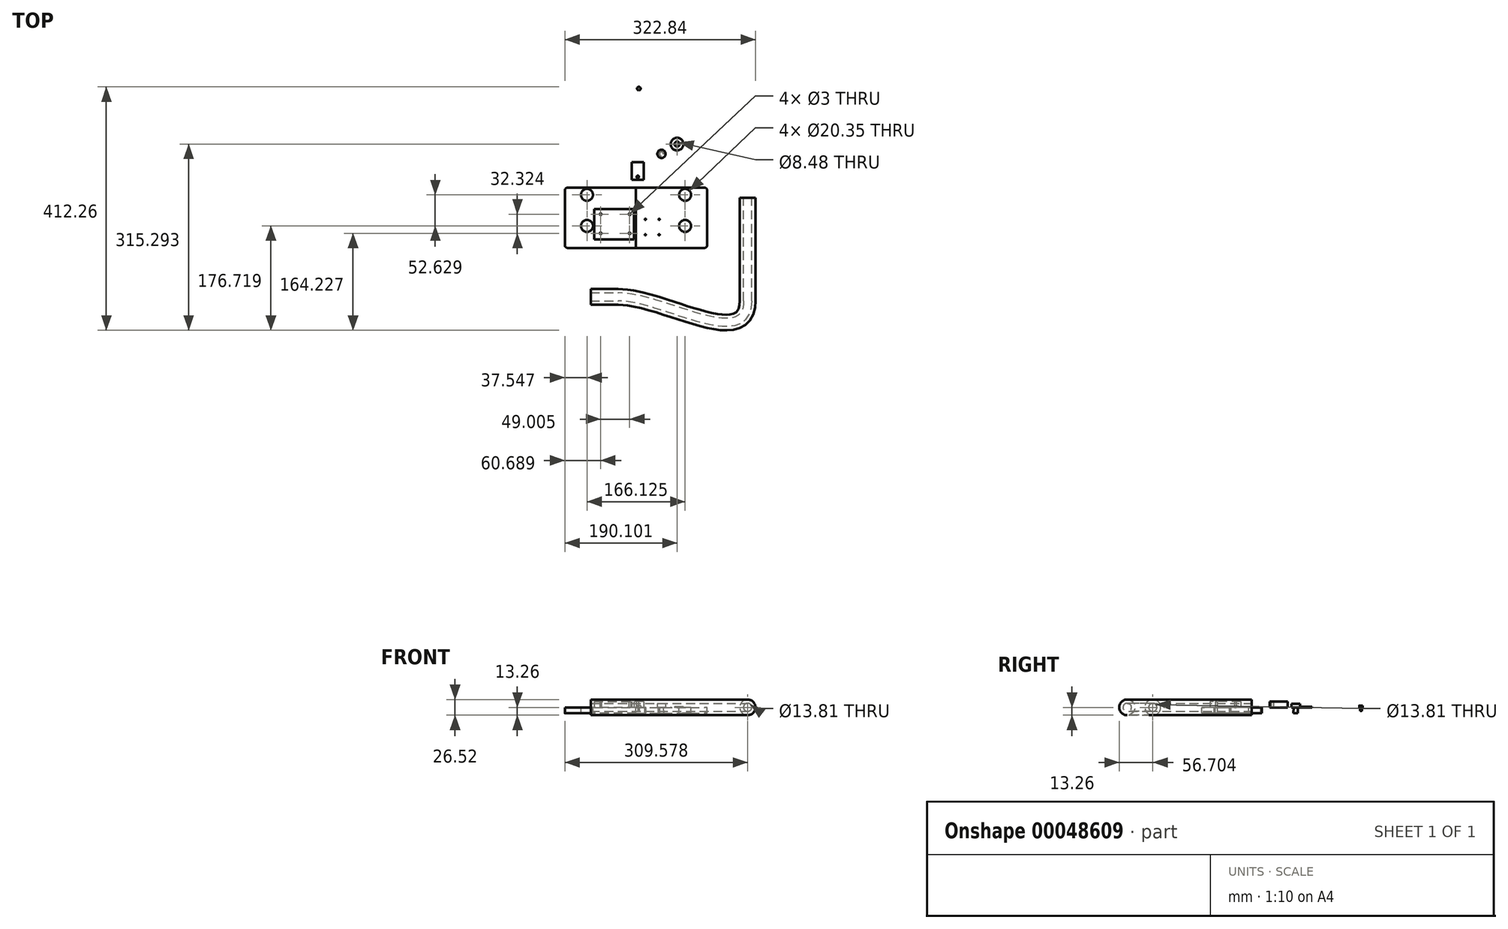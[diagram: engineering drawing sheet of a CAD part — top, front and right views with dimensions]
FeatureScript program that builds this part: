
annotation { "Feature Type Name" : "Feature", "Feature Type Description" : "" }
export const myFeature = defineFeature(function(context is Context, id is Id, definition is map)
    precondition{}
    {
        {
            var Q0;
            Q0=qCreatedBy(makeId("Top.planeOp"),FACE);
            var sketch = newSketch(context, id + "F17", { "sketchPlane" : qUnion([Q0])});
            skLineSegment(sketch, "E0.bottom", {"start": v(10, -15) * mm, "end": v(-10, -15) * mm});
            skLineSegment(sketch, "E0.top", {"start": v(10, 15) * mm, "end": v(-10, 15) * mm});
            skLineSegment(sketch, "E0.left", {"start": v(10, -15) * mm, "end": v(10, 15) * mm});
            skLineSegment(sketch, "E0.right", {"start": v(-10, -15) * mm, "end": v(-10, 15) * mm});
            skLineSegment(sketch, "E1", {"start": v(-10, 15) * mm, "end": v(10, -15) * mm, "construction": true});
            skSolve(sketch);
        }
        {
            var Q0;
            Q0 = qSketchRegion(id + "F17", true);
            extrude(context, id + "F18", {"entities" : qUnion([Q0]), "depth" : 10 * mm});
        }
        {
            var Q0;
            Q0=qCreatedBy(makeId("Top.planeOp"),FACE);
            var sketch = newSketch(context, id + "F19", { "sketchPlane" : qUnion([Q0])});
            skCircle(sketch, "E2", {"center": v(40.06, 28.89) * mm, "radius": 7.04 * mm});
            skSolve(sketch);
        }
        {
            var Q0;
            Q0=makeQuery(id+"F19.imprint","IMPRINT",FACE,{"disambiguationData":[TD([[makeQuery(id+"F19.imprint","IMPRINT",EDGE,{"derivedFrom":sQuery(id+"F19.wireOp",EDGE,"E2")}),1.0]])]});
            extrude(context, id + "F20", {"entities" : qUnion([Q0]), "depth" : 6 * mm});
        }
        {
            var Q0;
            Q0=makeQuery(id+"F20.opExtrude","CAP_FACE",FACE,{"disambiguationData":[OSD([sQuery(id+"F19.wireOp",EDGE,"E2")])],"isStart":true});
            var sketch = newSketch(context, id + "F0", { "sketchPlane" : qUnion([Q0])});
            skCircle(sketch, "E3", {"center": v(40.06, -28.89) * mm, "radius": 3.3 * mm});
            skSolve(sketch);
        }
        {
            var Q0;
            Q0 = qSketchRegion(id + "F0", true);
            extrude(context, id + "F21", {"entities" : qUnion([Q0]), "operationType" : NewBodyOperationType.ADD, "depth" : 10 * mm, "hasDraft" : true, "draftAngle" : 3 * degree});
        }
        {
            var Q0;
            Q0=makeQuery(id+"F18.opExtrude","CAP_FACE",FACE,{"disambiguationData":[OSD([sQuery(id+"F17.wireOp",EDGE,"E0.bottom"),sQuery(id+"F17.wireOp",EDGE,"E0.top"),sQuery(id+"F17.wireOp",EDGE,"E0.left"),sQuery(id+"F17.wireOp",EDGE,"E0.right")])],"isStart":false});
            var sketch = newSketch(context, id + "F1", { "sketchPlane" : qUnion([Q0])});
            skCircle(sketch, "E4", {"center": v(0, -10) * mm, "radius": 2 * mm});
            skSolve(sketch);
        }
        {
            var Q0;
            Q0 = qSketchRegion(id + "F1", true);
            extrude(context, id + "F22", {"entities" : qUnion([Q0]), "operationType" : NewBodyOperationType.REMOVE, "endBound" : BoundingType.THROUGH_ALL, "oppositeDirection" : true, "depth" : 25 * mm});
        }
        {
            var Q0;
            Q0=qCreatedBy(makeId("Top.planeOp"),FACE);
            var sketch = newSketch(context, id + "F2", { "sketchPlane" : qUnion([Q0])});
            skCircle(sketch, "E5", {"center": v(66.46, 45.41) * mm, "radius": 10.8 * mm});
            skCircle(sketch, "E6", {"center": v(66.46, 45.41) * mm, "radius": 4.24 * mm});
            skSolve(sketch);
        }
        {
            var Q0;
            Q0=makeQuery(id+"F2.imprint","IMPRINT",FACE,{"disambiguationData":[TD([[makeQuery(id+"F2.imprint","IMPRINT",EDGE,{"derivedFrom":sQuery(id+"F2.wireOp",EDGE,"E5")}),1.0]])]});
            var Q1;
            Q1=sQuery(id+"F2.wireOp",EDGE,"E6");
            extrude(context, id + "F23", {"entities" : qUnion([Q0]), "surfaceEntities" : qUnion([Q1]), "depth" : 1 * mm});
        }
        {
            var Q0;
            Q0=qCreatedBy(makeId("Top.planeOp"),FACE);
            var sketch = newSketch(context, id + "F24", { "sketchPlane" : qUnion([Q0])});
            skLineSegment(sketch, "E7", {"start": v(15.09, -40.53) * mm, "end": v(80.03, -40.53) * mm, "construction": true});
            skLineSegment(sketch, "E8", {"start": v(80.03, -40.53) * mm, "end": v(80.03, -93.16) * mm, "construction": true});
            skLineSegment(sketch, "E9", {"start": v(80.03, -93.16) * mm, "end": v(55.86, -93.16) * mm, "construction": true});
            skLineSegment(sketch, "E10", {"start": v(55.86, -93.16) * mm, "end": v(55.86, -62.33) * mm, "construction": true});
            skLineSegment(sketch, "E11", {"start": v(55.86, -62.33) * mm, "end": v(15.09, -62.33) * mm, "construction": true});
            skLineSegment(sketch, "E12", {"start": v(15.09, -62.33) * mm, "end": v(15.09, -40.53) * mm, "construction": true});
            skLineSegment(sketch, "E13.bottom", {"start": v(-3.03, -28.4) * mm, "end": v(117.58, -28.4) * mm});
            skLineSegment(sketch, "E13.top", {"start": v(-3.03, -130.43) * mm, "end": v(117.58, -130.43) * mm});
            skLineSegment(sketch, "E13.left", {"start": v(-3.03, -28.4) * mm, "end": v(-3.03, -130.43) * mm});
            skLineSegment(sketch, "E13.right", {"start": v(117.58, -28.4) * mm, "end": v(117.58, -130.43) * mm});
            skSolve(sketch);
        }
        {
            var Q0;
            Q0=qCreatedBy(makeId("Top.planeOp"),FACE);
            var sketch = newSketch(context, id + "F25", { "sketchPlane" : qUnion([Q0])});
            skCircle(sketch, "E14", {"center": v(80.03, -93.16) * mm, "radius": 10.18 * mm});
            skCircle(sketch, "E15", {"center": v(80.03, -40.53) * mm, "radius": 10.18 * mm});
            skSolve(sketch);
        }
        {
            var Q0;
            Q0=makeQuery(id+"F24.imprint","IMPRINT",FACE,{"disambiguationData":[TD([[makeQuery(id+"F24.imprint","IMPRINT",EDGE,{"derivedFrom":sQuery(id+"F24.wireOp",EDGE,"E13.bottom")}),-1.0]])]});
            extrude(context, id + "F3", {"entities" : qUnion([Q0]), "oppositeDirection" : true, "depth" : 10 * mm});
        }
        {
            var Q0;
            Q0 = qSketchRegion(id + "F25", true);
            extrude(context, id + "F26", {"entities" : qUnion([Q0]), "operationType" : NewBodyOperationType.REMOVE, "oppositeDirection" : true, "depth" : 25 * mm});
        }
        {
            var Q0;
            Q0=makeQuery(id+"F3.opExtrude","SWEPT_EDGE",EDGE,{"disambiguationData":[OSD([sQuery(id+"F24.wireOp",EDGE,"E13.top"),sQuery(id+"F24.wireOp",EDGE,"E13.right")])]});
            var Q1;
            Q1=makeQuery(id+"F3.opExtrude","SWEPT_EDGE",EDGE,{"disambiguationData":[OSD([sQuery(id+"F24.wireOp",EDGE,"E13.bottom"),sQuery(id+"F24.wireOp",EDGE,"E13.right")])]});
            fillet(context, id + "F4", {"entities" : qUnion([Q0, Q1]), "radius" : 5 * mm, "tangentPropagation" : true, "allowEdgeOverflow" : false});
        }
        {
            var Q0;
            Q0=makeQuery(id+"F3.opExtrude","SWEPT_BODY",BODY,{"disambiguationData":[OSD([sQuery(id+"F24.wireOp",EDGE,"E13.bottom"),sQuery(id+"F24.wireOp",EDGE,"E13.top"),sQuery(id+"F24.wireOp",EDGE,"E13.left"),sQuery(id+"F24.wireOp",EDGE,"E13.right")])]});
            var Q1;
            Q1=makeQuery(id+"F3.opExtrude","SWEPT_FACE",FACE,{"disambiguationData":[OSD([sQuery(id+"F24.wireOp",EDGE,"E13.left")])]});
            mirror(context, id + "F27", {"operationType" : NewBodyOperationType.ADD, "entities" : qUnion([Q0]), "mirrorPlane" : qUnion([Q1])});
        }
        {
            var Q0;
            Q0=qCreatedBy(makeId("Top.planeOp"),FACE);
            var sketch = newSketch(context, id + "F28", { "sketchPlane" : qUnion([Q0])});
            skLineSegment(sketch, "E16", {"start": v(-79.63, -213.18) * mm, "end": v(-33.15, -213.18) * mm});
            skLineSegment(sketch, "E17", {"start": v(185.94, -45.6) * mm, "end": v(185.94, -219.95) * mm});
            skFitSpline(sketch, "E18", {"points": [v(-33.15, -213.18) * mm, v(185.94, -219.95) * mm], "startDerivative": vector(229, 0) * mm, "endDerivative": vector(0, 258.85) * mm});
            skSolve(sketch);
        }
        {
            var Q0;
            Q0=sQuery(id+"F28.wireOp",VERTEX,"E16.start");
            var Q1;
            Q1=qCreatedBy(makeId("Right.planeOp"),FACE);
            cPlane(context, id + "F5", {"entities" : qUnion([Q0, Q1]), "cplaneType" : CPlaneType.PLANE_POINT, "offset" : 150 * mm, "width" : 150 * mm, "height" : 150 * mm});
        }
        {
            var Q0;
            Q0=qCreatedBy(id+"F5.planeOp",FACE);
            var sketch = newSketch(context, id + "F29", { "sketchPlane" : qUnion([Q0])});
            skCircle(sketch, "E19", {"center": v(-213.18, 0) * mm, "radius": 6.9 * mm});
            skCircle(sketch, "E20", {"center": v(-213.18, 0) * mm, "radius": 13.26 * mm});
            skSolve(sketch);
        }
        {
            var Q0;
            Q0 = qSketchRegion(id + "F29", true);
            var Q1;
            Q1=sQuery(id+"F28.wireOp",EDGE,"E16");
            var Q2;
            Q2=sQuery(id+"F28.wireOp",EDGE,"E18");
            var Q3;
            Q3=sQuery(id+"F28.wireOp",EDGE,"E17");
            sweep(context, id + "F30", {"profiles" : qUnion([Q0]), "path" : qUnion([Q1, Q2, Q3])});
        }
        {
            var Q0;
            {var subQ0=makeQuery(id+"F3.opExtrude","CAP_FACE",FACE,{"disambiguationData":[OSD([sQuery(id+"F24.wireOp",EDGE,"E13.bottom"),sQuery(id+"F24.wireOp",EDGE,"E13.top"),sQuery(id+"F24.wireOp",EDGE,"E13.left"),sQuery(id+"F24.wireOp",EDGE,"E13.right")])],"isStart":true});Q0=makeQuery(id+"F27.boolean.opBoolean","MERGE",FACE,{"derivedFrom":[subQ0,makeQuery(id+"F27.opPattern","COPY",FACE,{"derivedFrom":subQ0,"instanceName":"1"})]});}
            var sketch = newSketch(context, id + "F6", { "sketchPlane" : qUnion([Q0])});
            skLineSegment(sketch, "E21.bottom", {"start": v(-62.95, -73.33) * mm, "end": v(-13.95, -73.33) * mm});
            skLineSegment(sketch, "E21.top", {"start": v(-62.95, -105.65) * mm, "end": v(-13.95, -105.65) * mm});
            skLineSegment(sketch, "E21.left", {"start": v(-62.95, -73.33) * mm, "end": v(-62.95, -105.65) * mm});
            skLineSegment(sketch, "E21.right", {"start": v(-13.95, -73.33) * mm, "end": v(-13.95, -105.65) * mm});
            skSolve(sketch);
        }
        {
            var Q0;
            Q0=sQuery(id+"F6.wireOp",VERTEX,"E21.left.start");
            var Q1;
            Q1=sQuery(id+"F6.wireOp",VERTEX,"E21.right.start");
            var Q2;
            Q2=sQuery(id+"F6.wireOp",VERTEX,"E21.right.end");
            var Q3;
            Q3=sQuery(id+"F6.wireOp",VERTEX,"E21.top.start");
            var Q4;
            Q4=makeQuery(id+"F3.opExtrude","SWEPT_BODY",BODY,{"disambiguationData":[OSD([sQuery(id+"F24.wireOp",EDGE,"E13.bottom"),sQuery(id+"F24.wireOp",EDGE,"E13.top"),sQuery(id+"F24.wireOp",EDGE,"E13.left"),sQuery(id+"F24.wireOp",EDGE,"E13.right")])]});
            hole(context, id + "F7", {"style" : HoleStyle.C_BORE, "endStyle" : HoleEndStyle.THROUGH, "standardTappedOrClearance" : lookupTablePath({ "standard" : "ISO", "fit" : "Normal", "size" : "M3", "type" : "Clearance" }), "standardBlindInLast" : lookupTablePath({ "fit" : "Standard", "standard" : "ISO", "size" : "M3", "type" : "Clearance" }), "holeDiameter" : 3.3 * mm, "cBoreDiameter" : 6.5 * mm, "cBoreDepth" : 3 * mm, "isTappedThrough" : true, "tappedDepth" : 12 * mm, "tapClearance" : 3, "locations" : qUnion([Q0, Q1, Q2, Q3]), "scope" : qUnion([Q4])});
        }
        {
            var Q0;
            Q0=makeQuery(id+"F20.opExtrude","SWEPT_BODY",BODY,{"disambiguationData":[OSD([sQuery(id+"F19.wireOp",EDGE,"E2")])]});
            transform(context, id + "F8", {"entities" : qUnion([Q0]), "transformType" : TransformType.TRANSLATION_3D, "dx" : 0 * mm, "dy" : 0 * mm, "dz" : 0 * mm, "makeCopy" : true});
        }
        {
            var Q0;
            Q0=makeQuery(id+"F8.opPattern","COPY",BODY,{"derivedFrom":makeQuery(id+"F20.opExtrude","SWEPT_BODY",BODY,{"disambiguationData":[OSD([sQuery(id+"F19.wireOp",EDGE,"E2")])]}),"instanceName":"1"});
            deleteBodies(context, id + "F9", {"entities" : qUnion([Q0])});
        }
        {
            var Q0;
            Q0=qCreatedBy(makeId("Top.planeOp"),FACE);
            var sketch = newSketch(context, id + "F10", { "sketchPlane" : qUnion([Q0])});
            skCircle(sketch, "E22", {"center": v(1.78, 139.38) * mm, "radius": 3 * mm});
            skCircle(sketch, "E23", {"center": v(1.78, 139.38) * mm, "radius": 1.5 * mm});
            skSolve(sketch);
        }
        {
            var Q0;
            Q0=makeQuery(id+"F10.imprint","IMPRINT",FACE,{"disambiguationData":[TD([[makeQuery(id+"F10.imprint","IMPRINT",EDGE,{"derivedFrom":sQuery(id+"F10.wireOp",EDGE,"E23")}),1.0]])]});
            var Q1;
            Q1=makeQuery(id+"F10.imprint","IMPRINT",FACE,{"disambiguationData":[TD([[makeQuery(id+"F10.imprint","IMPRINT",EDGE,{"derivedFrom":sQuery(id+"F10.wireOp",EDGE,"E22")}),1.0]])]});
            extrude(context, id + "F11", {"entities" : qUnion([Q0, Q1]), "depth" : 3 * mm});
        }
        {
            var Q0;
            Q0=makeQuery(id+"F10.imprint","IMPRINT",FACE,{"disambiguationData":[TD([[makeQuery(id+"F10.imprint","IMPRINT",EDGE,{"derivedFrom":sQuery(id+"F10.wireOp",EDGE,"E23")}),1.0]])]});
            extrude(context, id + "F12", {"entities" : qUnion([Q0]), "operationType" : NewBodyOperationType.ADD, "oppositeDirection" : true, "depth" : 6 * mm});
        }
        {
            var Q0;
            {var subQ0=makeQuery(id+"F3.opExtrude","CAP_FACE",FACE,{"disambiguationData":[OSD([sQuery(id+"F24.wireOp",EDGE,"E13.bottom"),sQuery(id+"F24.wireOp",EDGE,"E13.top"),sQuery(id+"F24.wireOp",EDGE,"E13.left"),sQuery(id+"F24.wireOp",EDGE,"E13.right")])],"isStart":true});Q0=makeQuery(id+"F27.boolean.opBoolean","MERGE",FACE,{"derivedFrom":[subQ0,makeQuery(id+"F27.opPattern","COPY",FACE,{"derivedFrom":subQ0,"instanceName":"1"})]});}
            var sketch = newSketch(context, id + "F13", { "sketchPlane" : qUnion([Q0])});
            skLineSegment(sketch, "E24.bottom", {"start": v(-73.9, -64.37) * mm, "end": v(-6.2, -64.37) * mm});
            skLineSegment(sketch, "E24.top", {"start": v(-73.9, -116.08) * mm, "end": v(-6.2, -116.08) * mm});
            skLineSegment(sketch, "E24.left", {"start": v(-73.9, -64.37) * mm, "end": v(-73.9, -116.08) * mm});
            skLineSegment(sketch, "E24.right", {"start": v(-6.2, -64.37) * mm, "end": v(-6.2, -116.08) * mm});
            skCircle(sketch, "E25", {"center": v(-62.95, -73.33) * mm, "radius": 1.5 * mm});
            skCircle(sketch, "E26", {"center": v(-62.95, -105.65) * mm, "radius": 1.5 * mm});
            skCircle(sketch, "E27", {"center": v(-13.95, -73.33) * mm, "radius": 1.5 * mm});
            skCircle(sketch, "E28", {"center": v(-13.95, -105.65) * mm, "radius": 1.5 * mm});
            skSolve(sketch);
        }
        {
            var Q0;
            Q0=makeQuery(id+"F13.imprint","IMPRINT",FACE,{"disambiguationData":[TD([[makeQuery(id+"F13.imprint","IMPRINT",EDGE,{"derivedFrom":sQuery(id+"F13.wireOp",EDGE,"E24.bottom")}),-1.0]])]});
            var Q1;
            Q1=makeQuery(id+"F13.imprint","IMPRINT",FACE,{"disambiguationData":[TD([[makeQuery(id+"F13.imprint","IMPRINT",EDGE,{"derivedFrom":sQuery(id+"F13.wireOp",EDGE,"E26")}),-1.0]])]});
            var Q2;
            Q2=makeQuery(id+"F13.imprint","IMPRINT",FACE,{"disambiguationData":[TD([[makeQuery(id+"F13.imprint","IMPRINT",EDGE,{"derivedFrom":sQuery(id+"F13.wireOp",EDGE,"E27")}),-1.0]])]});
            var Q3;
            Q3=makeQuery(id+"F13.imprint","IMPRINT",FACE,{"disambiguationData":[TD([[makeQuery(id+"F13.imprint","IMPRINT",EDGE,{"derivedFrom":sQuery(id+"F13.wireOp",EDGE,"E28")}),-1.0]])]});
            var Q4;
            Q4=makeQuery(id+"F13.imprint","IMPRINT",FACE,{"disambiguationData":[TD([[makeQuery(id+"F13.imprint","IMPRINT",EDGE,{"derivedFrom":sQuery(id+"F13.wireOp",EDGE,"E25")}),-1.0]])]});
            extrude(context, id + "F14", {"entities" : qUnion([Q0, Q1, Q2, Q3, Q4]), "depth" : 10 * mm});
        }
        {
            var Q0;
            {var subQ0=makeQuery(id+"F3.opExtrude","CAP_FACE",FACE,{"disambiguationData":[OSD([sQuery(id+"F24.wireOp",EDGE,"E13.bottom"),sQuery(id+"F24.wireOp",EDGE,"E13.top"),sQuery(id+"F24.wireOp",EDGE,"E13.left"),sQuery(id+"F24.wireOp",EDGE,"E13.right")])],"isStart":true});Q0=makeQuery(id+"F27.boolean.opBoolean","MERGE",FACE,{"derivedFrom":[subQ0,makeQuery(id+"F27.opPattern","COPY",FACE,{"derivedFrom":subQ0,"instanceName":"1"})]});}
            var sketch = newSketch(context, id + "F15", { "sketchPlane" : qUnion([Q0])});
            skLineSegment(sketch, "E29.bottom", {"start": v(12.72, -81.79) * mm, "end": v(36.1, -81.79) * mm});
            skLineSegment(sketch, "E29.top", {"start": v(12.72, -108.12) * mm, "end": v(36.1, -108.12) * mm});
            skLineSegment(sketch, "E29.left", {"start": v(12.72, -81.79) * mm, "end": v(12.72, -108.12) * mm});
            skLineSegment(sketch, "E29.right", {"start": v(36.1, -81.79) * mm, "end": v(36.1, -108.12) * mm});
            skSolve(sketch);
        }
        {
            var Q0;
            Q0=sQuery(id+"F15.wireOp",VERTEX,"E29.left.start");
            var Q1;
            Q1=sQuery(id+"F15.wireOp",VERTEX,"E29.right.start");
            var Q2;
            Q2=sQuery(id+"F15.wireOp",VERTEX,"E29.left.end");
            var Q3;
            Q3=sQuery(id+"F15.wireOp",VERTEX,"E29.top.end");
            var Q4;
            Q4=makeQuery(id+"F3.opExtrude","SWEPT_BODY",BODY,{"disambiguationData":[OSD([sQuery(id+"F24.wireOp",EDGE,"E13.bottom"),sQuery(id+"F24.wireOp",EDGE,"E13.top"),sQuery(id+"F24.wireOp",EDGE,"E13.left"),sQuery(id+"F24.wireOp",EDGE,"E13.right")])]});
            hole(context, id + "F16", {"style" : HoleStyle.SIMPLE, "endStyle" : HoleEndStyle.THROUGH, "holeDiameter" : 2 * mm, "isTappedThrough" : true, "tappedDepth" : 12 * mm, "tapClearance" : 3, "locations" : qUnion([Q0, Q1, Q2, Q3]), "scope" : qUnion([Q4])});
        }
    });
